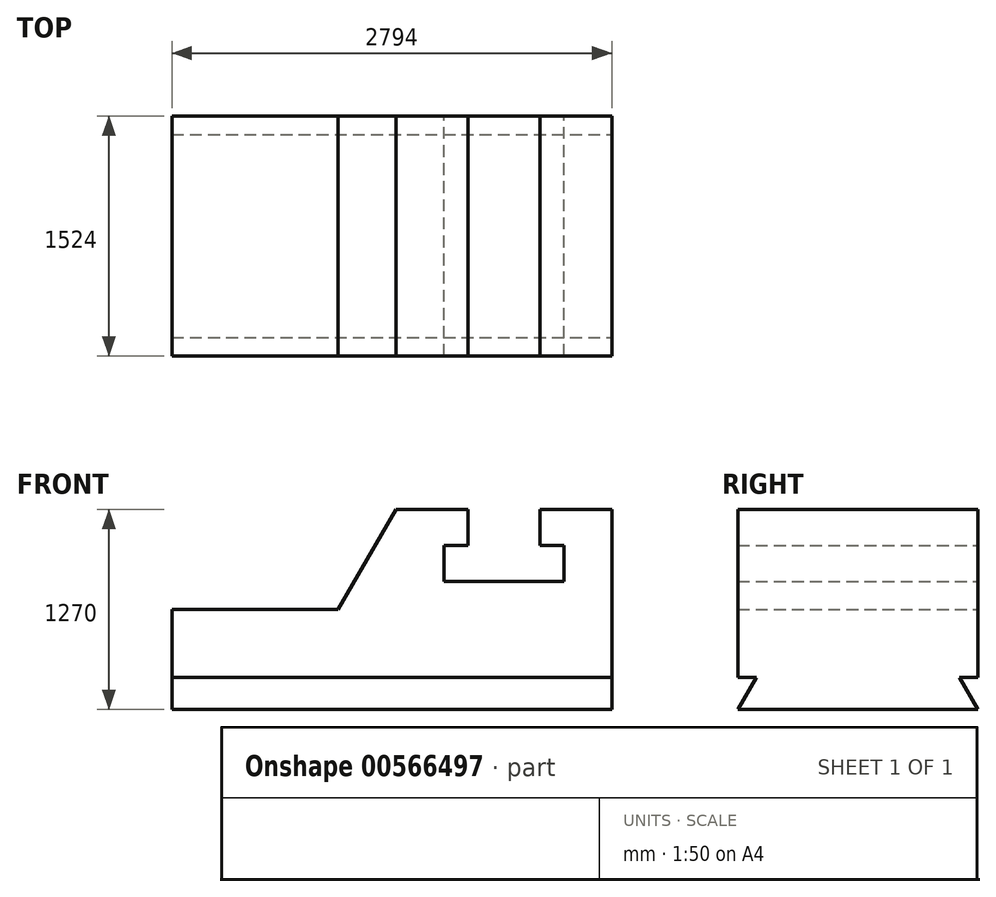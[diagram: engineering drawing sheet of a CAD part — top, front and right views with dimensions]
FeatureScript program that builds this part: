
annotation { "Feature Type Name" : "Feature", "Feature Type Description" : "" }
export const myFeature = defineFeature(function(context is Context, id is Id, definition is map)
    precondition{}
    {
        {
            var Q0;
            Q0=qCreatedBy(makeId("Front.planeOp"),FACE);
            var sketch = newSketch(context, id + "F0", { "sketchPlane" : qUnion([Q0])});
            skLineSegment(sketch, "E0", {"start": v(-1339.18, -735.08) * mm, "end": v(1454.82, -735.08) * mm});
            skLineSegment(sketch, "E1", {"start": v(1454.82, -735.08) * mm, "end": v(1454.82, 534.92) * mm});
            skLineSegment(sketch, "E2", {"start": v(1454.82, 534.92) * mm, "end": v(997.62, 534.92) * mm});
            skLineSegment(sketch, "E3", {"start": v(997.62, 534.92) * mm, "end": v(997.62, 306.32) * mm});
            skLineSegment(sketch, "E4", {"start": v(997.62, 306.32) * mm, "end": v(1150.02, 306.32) * mm});
            skLineSegment(sketch, "E5", {"start": v(1150.02, 306.32) * mm, "end": v(1150.02, 77.72) * mm});
            skLineSegment(sketch, "E6", {"start": v(1150.02, 77.72) * mm, "end": v(388.02, 77.72) * mm});
            skLineSegment(sketch, "E7", {"start": v(388.02, 77.72) * mm, "end": v(388.02, 306.32) * mm});
            skLineSegment(sketch, "E8", {"start": v(388.02, 306.32) * mm, "end": v(540.42, 306.32) * mm});
            skLineSegment(sketch, "E9", {"start": v(540.42, 306.32) * mm, "end": v(540.42, 534.92) * mm});
            skLineSegment(sketch, "E10", {"start": v(540.42, 534.92) * mm, "end": v(83.22, 534.92) * mm});
            skLineSegment(sketch, "E11", {"start": v(-1339.18, -735.08) * mm, "end": v(-1339.18, -100.08) * mm});
            skLineSegment(sketch, "E12", {"start": v(-1339.18, -100.08) * mm, "end": v(-283.4, -100.08) * mm});
            skLineSegment(sketch, "E13", {"start": v(83.22, 534.92) * mm, "end": v(-283.4, -100.08) * mm});
            skPoint(sketch, "E14.orphan", {"position": v(83.22, -100.08) * mm});
            skSolve(sketch);
        }
        {
            var Q0;
            Q0 = qSketchRegion(id + "F0", true);
            extrude(context, id + "F1", {"entities" : qUnion([Q0]), "depth" : 1524 * mm, "offsetDistance" : 25.4 * mm});
        }
        {
            var Q0;
            Q0=makeQuery(id+"F1.opExtrude","SWEPT_FACE",FACE,{"disambiguationData":[OSD([sQuery(id+"F0.wireOp",EDGE,"E1")])]});
            var sketch = newSketch(context, id + "F2", { "sketchPlane" : qUnion([Q0])});
            skLineSegment(sketch, "E15", {"start": v(0, -735.08) * mm, "end": v(0, -531.88) * mm});
            skLineSegment(sketch, "E16", {"start": v(0, -531.88) * mm, "end": v(-117.32, -531.88) * mm});
            skLineSegment(sketch, "E17", {"start": v(0, -735.08) * mm, "end": v(-117.32, -531.88) * mm});
            skLineSegment(sketch, "E18", {"start": v(-1524, -735.08) * mm, "end": v(-1406.68, -531.88) * mm});
            skLineSegment(sketch, "E19.trimOffspring", {"start": v(-1406.68, -531.88) * mm, "end": v(-1524, -531.88) * mm});
            skSolve(sketch);
        }
        {
            var Q0;
            Q0=makeQuery(id+"F2.imprint","IMPRINT",FACE,{"disambiguationData":[TD([[makeQuery(id+"F2.imprint","IMPRINT",EDGE,{"derivedFrom":sQuery(id+"F2.wireOp",EDGE,"E15")}),1.0]])]});
            extrude(context, id + "F3", {"entities" : qUnion([Q0]), "operationType" : NewBodyOperationType.REMOVE, "endBound" : BoundingType.THROUGH_ALL, "oppositeDirection" : true, "depth" : 25.4 * mm, "offsetDistance" : 25.4 * mm});
        }
        {
            var Q0;
            Q0=makeQuery(id+"F1.opExtrude","SWEPT_FACE",FACE,{"disambiguationData":[OSD([sQuery(id+"F0.wireOp",EDGE,"E1")])]});
            var sketch = newSketch(context, id + "F4", { "sketchPlane" : qUnion([Q0])});
            skLineSegment(sketch, "E20", {"start": v(-1524, -735.08) * mm, "end": v(-1406.68, -531.88) * mm});
            skLineSegment(sketch, "E21", {"start": v(-1406.68, -531.88) * mm, "end": v(-1524, -531.88) * mm});
            skSolve(sketch);
        }
        {
            var Q0;
            Q0 = qSketchRegion(id + "F4", true);
            var Q1;
            {var subQ0=sQuery(id+"F4.wireOp",EDGE,"E20");Q1=makeQuery(id+"F4.imprint","IMPRINT",FACE,{"disambiguationData":[TD([[makeQuery(id+"F4.imprint","IMPRINT",EDGE,{"derivedFrom":subQ0}),1.0]])]});}
            extrude(context, id + "F5", {"entities" : qUnion([Q0, Q1]), "operationType" : NewBodyOperationType.REMOVE, "endBound" : BoundingType.THROUGH_ALL, "oppositeDirection" : true, "depth" : 25.4 * mm, "offsetDistance" : 25.4 * mm});
        }
    });
